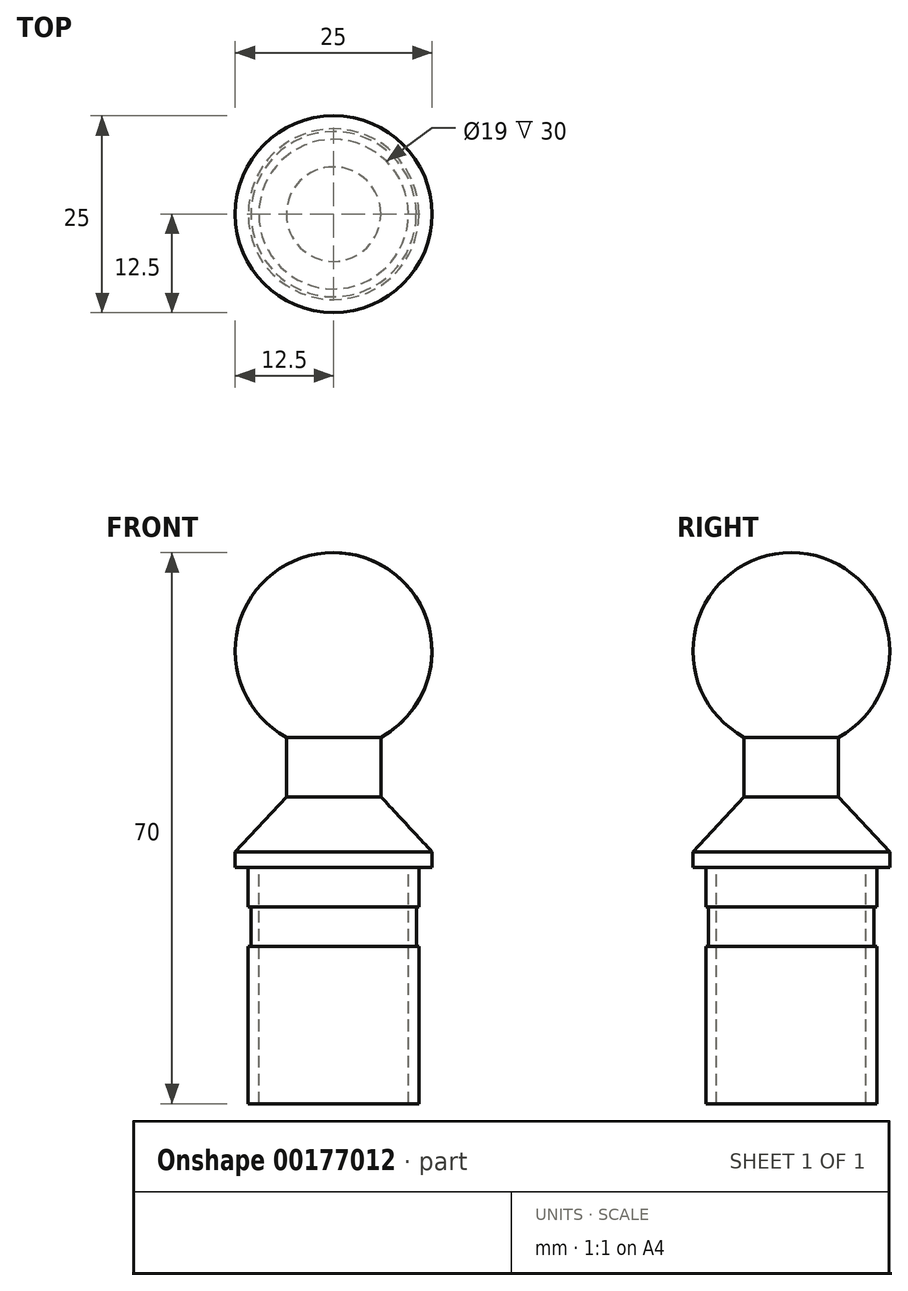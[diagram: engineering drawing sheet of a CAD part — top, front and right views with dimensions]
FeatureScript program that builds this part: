
annotation { "Feature Type Name" : "Feature", "Feature Type Description" : "" }
export const myFeature = defineFeature(function(context is Context, id is Id, definition is map)
    precondition{}
    {
        {
            var Q0;
            Q0=qCreatedBy(makeId("Front.planeOp"),FACE);
            var sketch = newSketch(context, id + "F0", { "sketchPlane" : qUnion([Q0])});
            skLineSegment(sketch, "E0", {"start": v(0, 32.72) * mm, "end": v(0, -7.28) * mm});
            skLineSegment(sketch, "E1.top", {"start": v(10.85, -37.28) * mm, "end": v(9.5, -37.28) * mm});
            skPoint(sketch, "E1.middle", {"position": v(0, 0) * mm});
            skLineSegment(sketch, "E2.left", {"start": v(10.85, -7.28) * mm, "end": v(10.85, -12.28) * mm});
            skLineSegment(sketch, "E3.trimOffspring", {"start": v(10.85, -7.28) * mm, "end": v(12.5, -7.28) * mm});
            skLineSegment(sketch, "E4.right", {"start": v(10.5, -12.28) * mm, "end": v(10.5, -17.28) * mm});
            skLineSegment(sketch, "E5", {"start": v(10.5, -17.28) * mm, "end": v(10.85, -17.28) * mm});
            skLineSegment(sketch, "E6", {"start": v(10.5, -12.28) * mm, "end": v(10.85, -12.28) * mm});
            skLineSegment(sketch, "E7.trimOffspring", {"start": v(10.85, -17.28) * mm, "end": v(10.85, -37.28) * mm});
            skLineSegment(sketch, "E8", {"start": v(9.5, -7.28) * mm, "end": v(9.5, -37.28) * mm});
            skLineSegment(sketch, "E9", {"start": v(9.5, -7.28) * mm, "end": v(0, -7.28) * mm});
            skPoint(sketch, "E10", {"position": v(12.5, -5.28) * mm});
            skLineSegment(sketch, "E11", {"start": v(6, 1.72) * mm, "end": v(12.5, -5.28) * mm});
            skArc(sketch, "E12", {"start": v(6, 9.25) * mm, "mid": v(12.11, 23.31) * mm, "end": v(0, 32.72) * mm});
            skLineSegment(sketch, "E13.trimOffspring", {"start": v(6, 9.25) * mm, "end": v(6, 1.72) * mm});
            skLineSegment(sketch, "E14.trimOffspring", {"start": v(12.5, -5.28) * mm, "end": v(12.5, -7.28) * mm});
            skPoint(sketch, "E15.orphan", {"position": v(0, 51.67) * mm});
            skLineSegment(sketch, "E16.trimOffspring", {"start": v(0, -7.28) * mm, "end": v(9.5, -7.28) * mm, "construction": true});
            skLineSegment(sketch, "E17.trimOffspring", {"start": v(10.85, -7.28) * mm, "end": v(12.5, -7.28) * mm, "construction": true});
            skSolve(sketch);
        }
        {
            var Q0;
            Q0=makeQuery(id+"F0.imprint","IMPRINT",FACE,{"disambiguationData":[TD([[makeQuery(id+"F0.imprint","IMPRINT",EDGE,{"derivedFrom":sQuery(id+"F0.wireOp",EDGE,"E0")}),1.0]])]});
            var Q1;
            Q1=sQuery(id+"F0.wireOp",EDGE,"E0");
            revolve(context, id + "F1", {"entities" : qUnion([Q0]), "axis" : qUnion([Q1]), "revolveType" : RevolveType.FULL});
        }
    });
